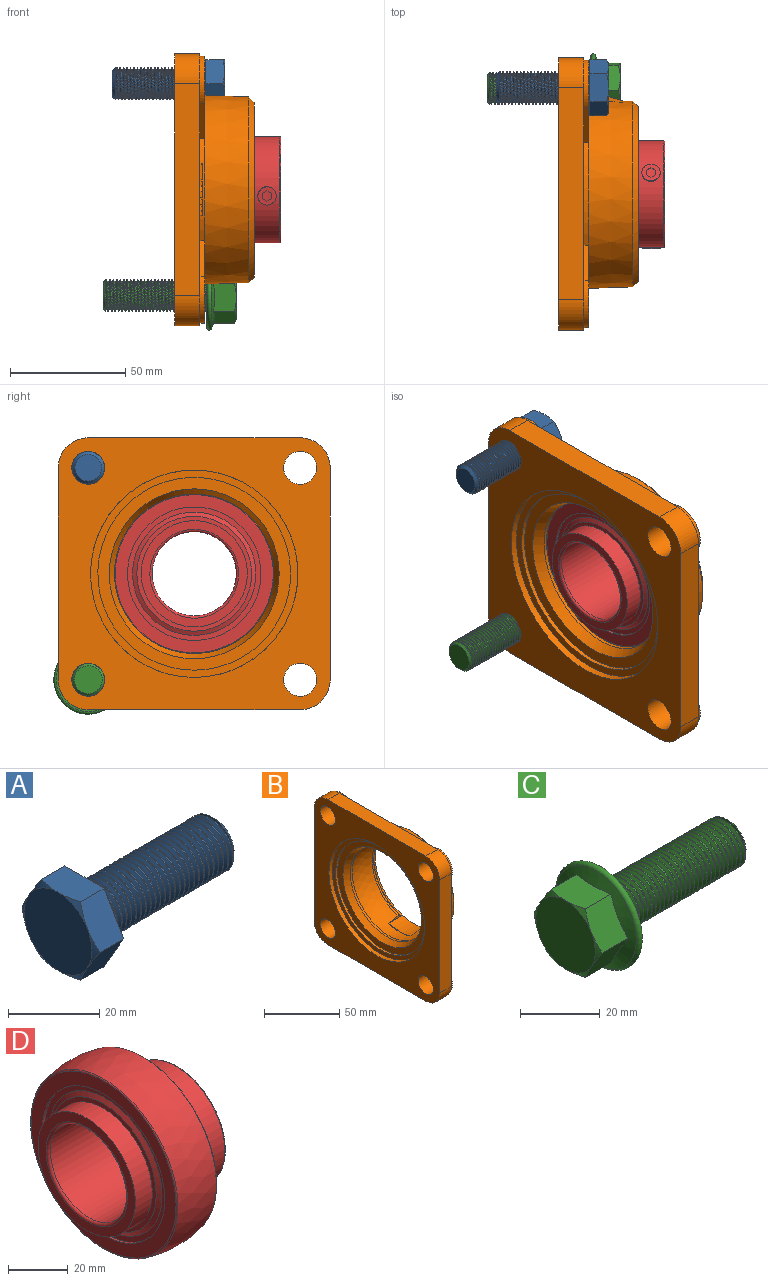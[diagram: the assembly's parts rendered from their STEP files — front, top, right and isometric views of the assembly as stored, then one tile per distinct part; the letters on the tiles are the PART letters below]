
ASSEMBLY  parts=4 mates=3
PART A: 25 faces, bbox 49.8x25.2x25.2 mm
  f0: plane 24.25x21mm, normal (1,0,0), area 87.2mm2, adj f1,f7,f8,f9,f10,f11,f12
  f1: cylinder r=9.68mm len=19.37mm, axis (1,0,0), area 36.5mm2, adj f0,f2
  f2: plane 19.37x19.37mm, normal (1,0,0), area 113.2mm2, adj f1,f3
  f3: torus R=7.6mm, axis (1,0,0), area 42.7mm2, adj f2,f4,f23
  f4: cylinder r=7mm len=38.17mm, axis (1,0,0), area 714.9mm2, adj f3,f5,f21,f22
  f5: cone r=7mm half-angle=45deg, axis (-1,0,0), area 69.6mm2, adj f4,f6,f24
  f6: plane 11.55x11.55mm, normal (1,0,0), area 104.7mm2, adj f5
  f7: plane 13.13x9.2mm, normal (0,0,1), area 95.5mm2, adj f0,f8,f12,f13,f14
  f8: plane 11.5x9.2mm, normal (0,0.87,0.5), area 95.5mm2, adj f0,f7,f9,f13,f17
  f9: plane 11.5x9.2mm, normal (0,0.87,-0.5), area 95.5mm2, adj f0,f8,f10,f16,f17
  f10: plane 13.13x9.2mm, normal (0,0,-1), area 95.5mm2, adj f0,f9,f11,f15,f16
  f11: plane 11.5x9.2mm, normal (0,-0.87,-0.5), area 95.5mm2, adj f0,f10,f12,f15,f19
  f12: plane 11.5x9.2mm, normal (0,-0.87,0.5), area 95.5mm2, adj f0,f7,f11,f14,f19
  f13: cone r=10.5mm half-angle=60deg, axis (1,0,0), area 10.8mm2, adj f7,f8,f18
  f14: cone r=10.5mm half-angle=60deg, axis (1,0,0), area 10.8mm2, adj f7,f12,f18
  f15: cone r=10.5mm half-angle=60deg, axis (1,0,0), area 10.8mm2, adj f10,f11,f18
  f16: cone r=10.5mm half-angle=60deg, axis (1,0,0), area 10.8mm2, adj f9,f10,f18
  f17: cone r=10.5mm half-angle=60deg, axis (1,0,0), area 10.8mm2, adj f8,f9,f18
  f18: plane 21x21mm, normal (-1,0,0), area 346.4mm2, adj f13,f14,f15,f16,f17,f19
  f19: cone r=10.5mm half-angle=60deg, axis (1,0,0), area 10.8mm2, adj f11,f12,f18
  f20: bspline ~39.13x14.29mm, area 409.6mm2, adj f21,f22,f23,f24
  f21: bspline ~39.47x16.17mm, area 983.8mm2, adj f4,f20,f23,f24
  f22: bspline ~39.22x16.17mm, area 995.1mm2, adj f4,f20,f23,f24
  f23: plane 14.46x14.08mm, normal (1,0,0), area 19.7mm2, adj f3,f20,f21,f22
  f24: plane 14.43x14.43mm, normal (-1,0,0), area 19.7mm2, adj f5,f20,f21,f22
PART B: 189 faces, bbox 34.7x118.2x118.2 mm
  f0: cone r=34.38mm half-angle=45deg, axis (1,0,0), area 159.3mm2, adj f2,f4,f183,f185
  f1: cone r=34.38mm half-angle=45deg, axis (1,0,0), area 159.3mm2, adj f3,f5,f182,f188
  f2: cylinder r=35.95mm len=68.8mm, axis (1,0,0), area 131.4mm2, adj f0,f178,f183,f185
  f3: cylinder r=35.95mm len=68.8mm, axis (1,0,0), area 131.4mm2, adj f1,f178,f182,f188
  f4: cylinder r=34.69mm len=66.17mm, axis (-1,0,0), area 122.5mm2, adj f0,f6,f183,f185
  f5: cylinder r=34.69mm len=66.17mm, axis (-1,0,0), area 122.5mm2, adj f1,f6,f182,f188
  f6: sphere r=35.95mm, area 3847.3mm2, adj f4,f5,f180,f181,f182,f183,f185,f186
  f7: cone r=36.85mm half-angle=24.3deg, axis (-1,0,0), area 1179.7mm2, adj f177,f180
  f8: plane 118x118mm, normal (1,0,0), area 4439.2mm2, adj f9,f11,f12,f13,f14,f15,f16,f17
  f9: cylinder r=45.07mm len=15.09mm, axis (1,0,0), area 32.1mm2, adj f8,f34,f36,f41
  f10: cylinder r=45mm len=90mm, axis (-1,0,0), area 904.8mm2, adj f19,f173
  f11: cylinder r=13mm len=13mm, axis (-1,0,0), area 224.7mm2, adj f8,f12,f18,f19
  f12: plane 92x11.01mm, normal (0,0,1), area 1012.5mm2, adj f8,f11,f13,f19
  f13: cylinder r=13mm len=13mm, axis (-1,0,0), area 224.7mm2, adj f8,f12,f14,f19
  f14: plane 92x11.01mm, normal (0,-1,0), area 1012.5mm2, adj f8,f13,f15,f19
  f15: cylinder r=13mm len=13mm, axis (-1,0,0), area 224.7mm2, adj f8,f14,f16,f19
  f16: plane 92x11.01mm, normal (0,0,-1), area 1012.5mm2, adj f8,f15,f17,f19
  f17: cylinder r=13mm len=13mm, axis (-1,0,0), area 224.7mm2, adj f8,f16,f18,f19
  f18: plane 92x11.01mm, normal (0,1,0), area 1012.5mm2, adj f8,f11,f17,f19
  f19: plane 118x118mm, normal (-1,0,0), area 6774.8mm2, adj f10,f11,f12,f13,f14,f15,f16,f17
  f20: plane 15.28x15.28mm, normal (0,0.71,-0.71), area 43.1mm2, adj f8,f21,f35,f36
  f21: cylinder r=12mm len=20.49mm, axis (1,0,0), area 75.2mm2, adj f8,f20,f22,f36
  f22: plane 15.28x15.28mm, normal (0,-0.71,0.71), area 43.1mm2, adj f8,f21,f23,f36
  f23: cylinder r=45.07mm len=44.47mm, axis (1,0,0), area 92.8mm2, adj f8,f22,f24,f36
  f24: plane 15.28x15.28mm, normal (0,0.71,0.71), area 43.1mm2, adj f8,f23,f25,f36
  f25: cylinder r=12mm len=20.49mm, axis (1,0,0), area 75.2mm2, adj f8,f24,f26,f36
  f26: plane 15.28x15.28mm, normal (0,-0.71,-0.71), area 43.1mm2, adj f8,f25,f27,f36
  f27: cylinder r=45.07mm len=44.47mm, axis (1,0,0), area 92.8mm2, adj f8,f26,f28,f36
  f28: plane 15.28x15.28mm, normal (0,-0.71,0.71), area 43.1mm2, adj f8,f27,f29,f36
  f29: cylinder r=12mm len=20.49mm, axis (1,0,0), area 75.2mm2, adj f8,f28,f30,f36
  f30: plane 15.28x15.28mm, normal (0,0.71,-0.71), area 43.1mm2, adj f8,f29,f31,f36
  f31: cylinder r=45.07mm len=44.47mm, axis (1,0,0), area 92.8mm2, adj f8,f30,f32,f36
  f32: plane 15.28x15.28mm, normal (0,-0.71,-0.71), area 43.1mm2, adj f8,f31,f33,f36
  f33: cylinder r=12mm len=20.49mm, axis (1,0,0), area 75.2mm2, adj f8,f32,f34,f36
  f34: plane 15.28x15.28mm, normal (0,0.71,0.71), area 43.1mm2, adj f8,f9,f33,f36
  f35: cylinder r=45.07mm len=15.09mm, axis (1,0,0), area 32.1mm2, adj f8,f20,f36,f40
  f36: plane 116x116mm, normal (1,0,0), area 3281mm2, adj f9,f20,f21,f22,f23,f24,f25,f26
  f37: cylinder r=7.15mm len=14.3mm, axis (-1,0,0), area 584mm2, adj f19,f36
  f38: cylinder r=7.15mm len=14.3mm, axis (-1,0,0), area 584mm2, adj f19,f36
  f39: cylinder r=7.15mm len=14.3mm, axis (-1,0,0), area 584mm2, adj f19,f36
  f40: plane 16.6x5.72mm, normal (0,0,1), area 39.7mm2, adj f8,f35,f36,f42,f43,f175
  f41: plane 16.6x5.72mm, normal (0,0,-1), area 39.7mm2, adj f8,f9,f36,f42,f43,f174
  f42: plane 14.3x0.65mm, normal (1,0,0), area 3.1mm2, adj f40,f41,f43,f174
  f43: plane 16.6x14.3mm, normal (0.29,0.96,0), area 221.4mm2, adj f8,f40,f41,f42,f44,f45,f46
  f44: plane 6.97x0.14mm, normal (1,0,0), area 0.6mm2, adj f43,f45
  f45: cylinder r=45.07mm len=6.97mm, axis (1,0,0), area 2.1mm2, adj f43,f44
  f46: cylinder r=2.8mm len=5.79mm, axis (0.29,0.96,0), area 26.4mm2, adj f43,f47
  f47: plane 5.6x5.36mm, normal (0.29,0.96,0), area 6.3mm2, adj f46,f48
  f48: torus R=2.42mm, axis (0.29,0.96,0), area 9.9mm2, adj f47,f49
  f49: cone r=1.78mm half-angle=32deg, axis (-0.29,-0.96,0), area 12.8mm2, adj f48,f50
  f50: cone r=1mm half-angle=32deg, axis (0.29,0.96,0), area 7.9mm2, adj f49,f51
  f51: torus R=0.68mm, axis (0.29,0.96,0), area 14.5mm2, adj f50,f52
  f52: cone r=1.3mm half-angle=51.3deg, axis (-0.29,-0.96,0), area 0.3mm2, adj f51,f53
  f53: torus R=0.65mm, axis (0.29,0.96,0), area 4.1mm2, adj f52,f54
  f54: plane 1.3x1.24mm, normal (0.29,0.96,0), area 0.5mm2, adj f53,f55
  f55: cylinder r=0.5mm len=1.1mm, axis (0.29,0.96,0), area 1.6mm2, adj f54,f56
  f56: sphere r=0.5mm, area 1.6mm2, adj f55
  f57: cylinder r=0.23mm len=1mm, axis (-1,0,0), area 0.4mm2, adj f8,f58,f170,f171
  f58: plane 1.63x1mm, normal (0,0,1), area 1.6mm2, adj f8,f57,f59,f171
  f59: cylinder r=0.23mm len=1mm, axis (-1,0,0), area 0.4mm2, adj f8,f58,f60,f171
  f60: plane 6.5x1mm, normal (0,-1,0), area 6.5mm2, adj f8,f59,f61,f171
  f61: cylinder r=0.23mm len=1mm, axis (-1,0,0), area 0.4mm2, adj f8,f60,f62,f171
  f62: plane 1x0.46mm, normal (0,-1,0), area 0.5mm2, adj f8,f61,f63,f171
  f63: cylinder r=0.23mm len=1mm, axis (-1,0,0), area 0.4mm2, adj f8,f62,f64,f171
  f64: plane 1.86x1mm, normal (0,-1,0), area 1.8mm2, adj f8,f63,f65,f171
  f65: cylinder r=0.23mm len=1mm, axis (-1,0,0), area 0.4mm2, adj f8,f64,f66,f171
  f66: plane 1.86x1mm, normal (0,0,-1), area 1.8mm2, adj f8,f65,f67,f171
  f67: plane 2.02x2.02mm, normal (0,-0.71,0.71), area 2.8mm2, adj f8,f66,f68,f171
  f68: cylinder r=0.23mm len=1mm, axis (-1,0,0), area 0.2mm2, adj f8,f67,f69,f171
  f69: plane 2.46x1mm, normal (0,-1,0), area 2.4mm2, adj f8,f68,f70,f171
  f70: cylinder r=0.23mm len=1mm, axis (-1,0,0), area 0.4mm2, adj f8,f69,f71,f171
  f71: plane 1x0.72mm, normal (0,-1,0), area 0.7mm2, adj f8,f70,f72,f171
  f72: cylinder r=0.23mm len=1mm, axis (-1,0,0), area 0.4mm2, adj f8,f71,f73,f171
  f73: plane 1.86x1mm, normal (0,-1,0), area 1.8mm2, adj f8,f72,f74,f171
  f74: cylinder r=0.23mm len=1mm, axis (-1,0,0), area 0.4mm2, adj f8,f73,f75,f171
  f75: plane 1.63x1mm, normal (0,0,-1), area 1.6mm2, adj f8,f74,f76,f171
  f76: cylinder r=0.23mm len=1mm, axis (-1,0,0), area 0.4mm2, adj f8,f75,f77,f171
  f77: cylinder r=0.23mm len=1mm, axis (-1,0,0), area 0.4mm2, adj f8,f76,f78,f171
  f78: plane 1x0.23mm, normal (0,0,-1), area 0.2mm2, adj f8,f77,f79,f171
  f79: cylinder r=0.23mm len=1mm, axis (-1,0,0), area 0.4mm2, adj f8,f78,f80,f171
  f80: plane 1x0.83mm, normal (0,-1,0), area 0.8mm2, adj f8,f79,f81,f171
  f81: cylinder r=0.23mm len=1mm, axis (-1,0,0), area 0.2mm2, adj f8,f80,f82,f171
  f82: plane 1x0.1mm, normal (0,-0.71,0.71), area 0.1mm2, adj f8,f81,f83,f171
  f83: cylinder r=0.23mm len=1mm, axis (-1,0,0), area 0.2mm2, adj f8,f82,f84,f171
  f84: plane 1.53x1mm, normal (0,-1,0), area 1.5mm2, adj f8,f83,f85,f171
  f85: cylinder r=0.23mm len=1mm, axis (-1,0,0), area 0.4mm2, adj f8,f84,f86,f171
  f86: plane 1x0.7mm, normal (0,0,-1), area 0.7mm2, adj f8,f85,f87,f171
  f87: cylinder r=0.23mm len=1mm, axis (-1,0,0), area 0.4mm2, adj f8,f86,f88,f171
  f88: plane 1.53x1mm, normal (0,1,0), area 1.5mm2, adj f8,f87,f89,f171
  f89: cylinder r=0.23mm len=1mm, axis (-1,0,0), area 0.2mm2, adj f8,f88,f90,f171
  f90: plane 1x0.1mm, normal (0,0.71,0.71), area 0.1mm2, adj f8,f89,f91,f171
  f91: cylinder r=0.23mm len=1mm, axis (-1,0,0), area 0.2mm2, adj f8,f90,f92,f171
  f92: plane 1x0.83mm, normal (0,1,0), area 0.8mm2, adj f8,f91,f93,f171
  f93: cylinder r=0.23mm len=1mm, axis (-1,0,0), area 0.4mm2, adj f8,f92,f94,f171
  f94: plane 1x0.83mm, normal (0,0,-1), area 0.8mm2, adj f8,f93,f95,f171
  f95: cylinder r=0.33mm len=1mm, axis (-1,0,0), area 0.5mm2, adj f8,f94,f96,f171
  f96: plane 1.99x1mm, normal (0,-1,0), area 2mm2, adj f8,f95,f97,f171
  f97: cylinder r=0.23mm len=1mm, axis (-1,0,0), area 0.4mm2, adj f8,f96,f98,f171
  f98: plane 1x0.23mm, normal (0,0,1), area 0.2mm2, adj f8,f97,f99,f171
  f99: cylinder r=0.23mm len=1mm, axis (-1,0,0), area 0.4mm2, adj f8,f98,f100,f171
  f100: plane 2.32x1mm, normal (0,-1,0), area 2.3mm2, adj f8,f99,f101,f171
  f101: cylinder r=0.23mm len=1mm, axis (-1,0,0), area 0.4mm2, adj f8,f100,f102,f171
  f102: plane 1x0.93mm, normal (0,0,-1), area 0.9mm2, adj f8,f101,f103,f171
  f103: cylinder r=0.23mm len=1mm, axis (-1,0,0), area 0.4mm2, adj f8,f102,f104,f171
  f104: plane 6.73x1mm, normal (0,1,0), area 6.7mm2, adj f8,f103,f105,f171
  f105: cylinder r=0.23mm len=1mm, axis (-1,0,0), area 0.4mm2, adj f8,f104,f106,f171
  f106: plane 1.53x1mm, normal (0,0,1), area 1.5mm2, adj f8,f105,f107,f171
  f107: cylinder r=0.23mm len=1mm, axis (-1,0,0), area 0.2mm2, adj f8,f106,f108,f171
  f108: plane 1x0.07mm, normal (0,-0.71,0.71), area 0.1mm2, adj f8,f107,f109,f171
  f109: cylinder r=0.33mm len=1mm, axis (-1,0,0), area 0.3mm2, adj f8,f108,f110,f171
  f110: plane 1.16x1mm, normal (0,0,1), area 1.2mm2, adj f8,f109,f111,f171
  f111: cylinder r=0.23mm len=1mm, axis (-1,0,0), area 0.2mm2, adj f8,f110,f112,f171
  f112: plane 1x0.1mm, normal (0,0.71,0.71), area 0.1mm2, adj f8,f111,f113,f171
  f113: cylinder r=0.23mm len=1mm, axis (-1,0,0), area 0.2mm2, adj f8,f112,f114,f171
  f114: plane 1.3x1mm, normal (0,0,1), area 1.3mm2, adj f8,f113,f115,f171
  f115: plane 1x0.72mm, normal (0,1,0), area 0.7mm2, adj f8,f114,f116,f171
  f116: plane 1.39x1mm, normal (0,0,-1), area 1.4mm2, adj f8,f115,f117,f171
  f117: cylinder r=0.23mm len=1mm, axis (-1,0,0), area 0.4mm2, adj f8,f116,f118,f171
  f118: plane 1.54x1mm, normal (0,1,0), area 1.5mm2, adj f8,f117,f119,f171
  f119: cylinder r=0.23mm len=1mm, axis (-1,0,0), area 0.2mm2, adj f8,f118,f120,f171
  f120: plane 1.56x1.34mm, normal (0,0.76,-0.65), area 2mm2, adj f8,f119,f121,f171
  f121: plane 1x0.63mm, normal (0,-0.71,-0.71), area 0.9mm2, adj f8,f120,f122,f171
  f122: cylinder r=0.23mm len=1mm, axis (-1,0,0), area 0.2mm2, adj f8,f121,f123,f171
  f123: plane 1.76x1mm, normal (0,-1,0), area 1.8mm2, adj f8,f122,f124,f171
  f124: cylinder r=0.23mm len=1mm, axis (-1,0,0), area 0.4mm2, adj f8,f123,f125,f171
  f125: plane 1x0.93mm, normal (0,0,-1), area 0.9mm2, adj f8,f124,f126,f171
  f126: cylinder r=0.23mm len=1mm, axis (-1,0,0), area 0.4mm2, adj f8,f125,f127,f171
  f127: plane 1.99x1mm, normal (0,1,0), area 2mm2, adj f8,f126,f128,f171
  f128: cylinder r=0.23mm len=1mm, axis (-1,0,0), area 0.2mm2, adj f8,f127,f129,f171
  f129: plane 2.01x1.79mm, normal (0,0.66,0.75), area 2.7mm2, adj f8,f128,f130,f171
  f130: plane 1.86x1mm, normal (0,0,-1), area 1.8mm2, adj f8,f129,f131,f171
  f131: cylinder r=0.23mm len=1mm, axis (-1,0,0), area 0.4mm2, adj f8,f130,f132,f171
  f132: plane 1.86x1mm, normal (0,1,0), area 1.8mm2, adj f8,f131,f133,f171
  f133: cylinder r=0.23mm len=1mm, axis (-1,0,0), area 0.4mm2, adj f8,f132,f134,f171
  f134: plane 1.53x1mm, normal (0,0,1), area 1.5mm2, adj f8,f133,f135,f171
  f135: cylinder r=0.23mm len=1mm, axis (-1,0,0), area 0.2mm2, adj f8,f134,f136,f171
  f136: plane 1x0.1mm, normal (0,-0.71,0.71), area 0.1mm2, adj f8,f135,f137,f171
  f137: cylinder r=0.23mm len=1mm, axis (-1,0,0), area 0.2mm2, adj f8,f136,f138,f171
  f138: plane 1x0.97mm, normal (0,0,1), area 1mm2, adj f8,f137,f139,f171
  f139: cylinder r=0.23mm len=1mm, axis (-1,0,0), area 0.2mm2, adj f8,f138,f140,f171
  f140: plane 1x0.1mm, normal (0,0.71,0.71), area 0.1mm2, adj f8,f139,f141,f171
  f141: cylinder r=0.23mm len=1mm, axis (-1,0,0), area 0.2mm2, adj f8,f140,f142,f171
  f142: plane 1.53x1mm, normal (0,0,1), area 1.5mm2, adj f8,f141,f143,f171
  f143: plane 1x0.46mm, normal (0,1,0), area 0.5mm2, adj f8,f142,f144,f171
  f144: plane 2.79x1mm, normal (0,0,-1), area 2.8mm2, adj f8,f143,f145,f171
  f145: cylinder r=0.23mm len=1mm, axis (-1,0,0), area 0.4mm2, adj f8,f144,f146,f171
  f146: plane 3.71x1mm, normal (0,1,0), area 3.7mm2, adj f8,f145,f147,f171
  f147: cylinder r=0.23mm len=1mm, axis (-1,0,0), area 0.4mm2, adj f8,f146,f148,f171
  f148: plane 1x0.93mm, normal (0,0,-1), area 0.9mm2, adj f8,f147,f149,f171
  f149: cylinder r=0.23mm len=1mm, axis (-1,0,0), area 0.4mm2, adj f8,f148,f150,f171
  f150: plane 1x0.93mm, normal (0,-1,0), area 0.9mm2, adj f8,f149,f151,f171
  f151: cylinder r=0.23mm len=1mm, axis (-1,0,0), area 0.4mm2, adj f8,f150,f152,f171
  f152: plane 1x0.23mm, normal (0,0,1), area 0.2mm2, adj f8,f151,f153,f171
  f153: cylinder r=0.23mm len=1mm, axis (-1,0,0), area 0.4mm2, adj f8,f152,f154,f171
  f154: plane 1.63x1mm, normal (0,-1,0), area 1.6mm2, adj f8,f153,f155,f171
  f155: cylinder r=0.23mm len=1mm, axis (-1,0,0), area 0.4mm2, adj f8,f154,f156,f171
  f156: plane 1x0.86mm, normal (0,0,-1), area 0.9mm2, adj f8,f155,f157,f171
  f157: cylinder r=0.3mm len=1mm, axis (-1,0,0), area 0.5mm2, adj f8,f156,f158,f171
  f158: plane 4.99x1mm, normal (0,1,0), area 5mm2, adj f8,f157,f159,f171
  f159: cylinder r=0.28mm len=1mm, axis (-1,0,0), area 0.4mm2, adj f8,f158,f160,f171
  f160: plane 2.27x1mm, normal (0,0,1), area 2.3mm2, adj f8,f159,f161,f171
  f161: cylinder r=0.23mm len=1mm, axis (-1,0,0), area 0.4mm2, adj f8,f160,f162,f171
  f162: plane 3.71x1mm, normal (0,-1,0), area 3.7mm2, adj f8,f161,f163,f171
  f163: cylinder r=0.23mm len=1mm, axis (-1,0,0), area 0.4mm2, adj f8,f162,f164,f171
  f164: plane 1.63x1mm, normal (0,0,1), area 1.6mm2, adj f8,f163,f165,f171
  f165: cylinder r=0.23mm len=1mm, axis (-1,0,0), area 0.4mm2, adj f8,f164,f166,f171
  f166: plane 2.32x1mm, normal (0,1,0), area 2.3mm2, adj f8,f165,f167,f171
  f167: cylinder r=0.23mm len=1mm, axis (-1,0,0), area 0.4mm2, adj f8,f166,f168,f171
  f168: plane 1x0.93mm, normal (0,0,-1), area 0.9mm2, adj f8,f167,f169,f171
  f169: cylinder r=0.23mm len=1mm, axis (-1,0,0), area 0.4mm2, adj f8,f168,f170,f171
  f170: plane 1.63x1mm, normal (0,1,0), area 1.6mm2, adj f8,f57,f169,f171
  f171: plane 22.54x5.57mm, normal (1,0,0), area 73.4mm2, adj f57,f58,f59,f60,f61,f62,f63,f64
  f172: cylinder r=7.15mm len=14.3mm, axis (-1,0,0), area 584mm2, adj f19,f36
  f173: plane 90x90mm, normal (-1,0,0), area 862.3mm2, adj f10,f176
  f174: cone r=40.3mm half-angle=2deg, axis (-1,0,0), area 4716.6mm2, adj f36,f41,f42,f175,f179
  f175: cone r=40.3mm half-angle=2deg, axis (-1,0,0), area 0.7mm2, adj f36,f40,f174
  f176: cylinder r=41.84mm len=83.68mm, axis (1,0,0), area 479.8mm2, adj f173,f177
  f177: plane 83.68x83.68mm, normal (-1,0,0), area 1232.3mm2, adj f7,f176
  f178: plane 76.18x76.18mm, normal (1,0,0), area 495.2mm2, adj f2,f3,f179,f182,f183,f184,f185,f187
  f179: cone r=38.09mm half-angle=45deg, axis (-1,0,0), area 771.5mm2, adj f174,f178
  f180: cylinder r=34.69mm len=69.39mm, axis (-1,0,0), area 386.9mm2, adj f6,f7
  f181: plane 20.9x1.6mm, normal (1,0,0), area 1.1mm2, adj f6,f182,f183,f184
  f182: plane 13.7x1.57mm, normal (0,1,0), area 7.5mm2, adj f1,f3,f5,f6,f178,f181,f184
  f183: plane 13.7x1.57mm, normal (0,-1,0), area 7.5mm2, adj f0,f2,f4,f6,f178,f181,f184
  f184: cylinder r=36mm len=20.9mm, axis (-1,0,0), area 286.3mm2, adj f178,f181,f182,f183
  f185: plane 13.7x1.57mm, normal (0,-1,0), area 7.5mm2, adj f0,f2,f4,f6,f178,f186,f187
  f186: plane 20.9x1.6mm, normal (1,0,0), area 1.1mm2, adj f6,f185,f187,f188
  f187: cylinder r=36mm len=20.9mm, axis (-1,0,0), area 286.3mm2, adj f178,f185,f186,f188
  f188: plane 13.7x1.57mm, normal (0,1,0), area 7.5mm2, adj f1,f3,f5,f6,f178,f186,f187
PART C: 25 faces, bbox 58.8x33.4x33.4 mm
  f0: plane 27.8x27.8mm, normal (1,0,0), area 425.5mm2, adj f1,f6
  f1: torus R=7.6mm, axis (1,0,0), area 42.7mm2, adj f0,f2,f23
  f2: cylinder r=7mm len=43.48mm, axis (1,0,0), area 664.9mm2, adj f1,f3,f21,f22
  f3: cone r=7mm half-angle=45deg, axis (-1,0,0), area 53.5mm2, adj f2,f4,f24
  f4: plane 12.16x12.16mm, normal (1,0,0), area 116.1mm2, adj f3
  f5: cone r=0mm half-angle=70deg, axis (1,0,0), area 273.3mm2, adj f6,f7,f8,f9,f10,f11,f12
  f6: torus R=13.9mm, axis (1,0,0), area 269.5mm2, adj f0,f5
  f7: plane 11.5x10.98mm, normal (0,-0.87,0.5), area 112.5mm2, adj f5,f8,f12,f13,f18
  f8: plane 11.5x10.98mm, normal (0,-0.87,-0.5), area 112.5mm2, adj f5,f7,f9,f17,f18
  f9: plane 13.13x10.99mm, normal (0,0,-1), area 112.5mm2, adj f5,f8,f10,f16,f17
  f10: plane 11.5x10.98mm, normal (0,0.87,-0.5), area 112.5mm2, adj f5,f9,f11,f15,f16
  f11: plane 11.5x10.98mm, normal (0,0.87,0.5), area 112.5mm2, adj f5,f10,f12,f14,f15
  f12: plane 13.13x10.99mm, normal (0,0,1), area 112.5mm2, adj f5,f7,f11,f13,f14
  f13: cone r=10.5mm half-angle=60deg, axis (1,0,0), area 10.8mm2, adj f7,f12,f19
  f14: cone r=10.5mm half-angle=60deg, axis (1,0,0), area 10.8mm2, adj f11,f12,f19
  f15: cone r=10.5mm half-angle=60deg, axis (1,0,0), area 10.8mm2, adj f10,f11,f19
  f16: cone r=10.5mm half-angle=60deg, axis (1,0,0), area 10.8mm2, adj f9,f10,f19
  f17: cone r=10.5mm half-angle=60deg, axis (1,0,0), area 10.8mm2, adj f8,f9,f19
  f18: cone r=10.5mm half-angle=60deg, axis (1,0,0), area 10.8mm2, adj f7,f8,f19
  f19: plane 21x21mm, normal (-1,0,0), area 346.4mm2, adj f13,f14,f15,f16,f17,f18
  f20: bspline ~44.63x14.29mm, area 466.9mm2, adj f21,f22,f23,f24
  f21: bspline ~44.72x16.17mm, area 1125.2mm2, adj f2,f20,f23,f24
  f22: bspline ~44.47x16.17mm, area 1131.5mm2, adj f2,f20,f23,f24
  f23: plane 14.45x14.42mm, normal (1,0,0), area 19.7mm2, adj f1,f20,f21,f22
  f24: plane 14.43x14.43mm, normal (-1,0,0), area 19.7mm2, adj f3,f20,f21,f22
PART D: 39 faces, bbox 42.9x75.4x75.4 mm
  f0: cylinder r=23.05mm len=46.1mm, axis (1,0,0), area 2130.8mm2, adj f6,f7,f27,f36
  f1: plane 46.1x46.1mm, normal (-1,0,0), area 504.2mm2, adj f2,f20
  f2: torus R=19.26mm, axis (1,0,0), area 183.8mm2, adj f1,f3
  f3: cylinder r=18.26mm len=40.9mm, axis (1,0,0), area 4691.5mm2, adj f2,f4
  f4: torus R=19.26mm, axis (1,0,0), area 183.8mm2, adj f3,f5
  f5: plane 45.1x45.1mm, normal (1,0,0), area 432.6mm2, adj f4,f6
  f6: torus R=22.55mm, axis (1,0,0), area 112.9mm2, adj f0,f5
  f7: plane 49.8x49.8mm, normal (1,0,0), area 278.7mm2, adj f0,f8
  f8: cone r=24.9mm half-angle=62.8deg, axis (-1,0,0), area 337.5mm2, adj f7,f9
  f9: plane 57.94x57.94mm, normal (1,0,0), area 389mm2, adj f8,f10
  f10: cylinder r=28.97mm len=57.94mm, axis (1,0,0), area 172.9mm2, adj f9,f11
  f11: plane 68.68x68.68mm, normal (1,0,0), area 1067.7mm2, adj f10,f12
  f12: torus R=34.34mm, axis (1,0,0), area 143mm2, adj f11,f13
  f13: sphere r=36mm, area 4128.8mm2, adj f12,f14
  f14: torus R=34.34mm, axis (1,0,0), area 143mm2, adj f13,f15
  f15: plane 68.68x68.68mm, normal (-1,0,0), area 1067.7mm2, adj f14,f16
  f16: cylinder r=28.97mm len=57.94mm, axis (1,0,0), area 172.9mm2, adj f15,f17
  f17: plane 57.94x57.94mm, normal (-1,0,0), area 389mm2, adj f16,f18
  f18: cone r=26.75mm half-angle=62.8deg, axis (1,0,0), area 337.5mm2, adj f17,f19
  f19: plane 49.8x49.8mm, normal (-1,0,0), area 278.7mm2, adj f18,f20
  f20: cylinder r=23.05mm len=46.1mm, axis (1,0,0), area 1158.6mm2, adj f1,f19
  f21: plane 2.29x0.51mm, normal (1,0,0), area 1.1mm2, adj f22,f26,f28,f29
  f22: plane 1.99x1.15mm, normal (0.5,0,0.87), area 1.3mm2, adj f21,f23,f28,f29
  f23: plane 1.99x1.15mm, normal (-0.5,0,0.87), area 1.3mm2, adj f22,f24,f28,f29
  f24: plane 2.29x0.51mm, normal (-1,0,0), area 1.1mm2, adj f23,f25,f28,f29
  f25: plane 1.99x1.15mm, normal (-0.5,0,-0.87), area 1.3mm2, adj f24,f26,f28,f29
  f26: plane 1.99x1.15mm, normal (0.5,0,-0.87), area 1.3mm2, adj f21,f25,f28,f29
  f27: cylinder r=3.97mm len=7.94mm, axis (0,-1,0), area 16.2mm2, adj f0,f28
  f28: plane 7.94x7.94mm, normal (0,1,0), area 35.8mm2, adj f21,f22,f23,f24,f25,f26,f27
  f29: cylinder r=23.05mm len=4.58mm, axis (1,0,0), area 13.7mm2, adj f21,f22,f23,f24,f25,f26
  f30: plane 2.24x1.59mm, normal (1,0,0), area 1.1mm2, adj f32,f35,f37,f38
  f31: plane 2.24x1.59mm, normal (-1,0,0), area 1.1mm2, adj f33,f34,f37,f38
  f32: plane 1.99x1.25mm, normal (0.5,0.75,-0.43), area 1.3mm2, adj f30,f33,f37,f38
  f33: plane 1.99x1.25mm, normal (-0.5,0.75,-0.43), area 1.3mm2, adj f31,f32,f37,f38
  f34: plane 1.99x1.29mm, normal (-0.5,-0.75,0.43), area 1.3mm2, adj f31,f35,f37,f38
  f35: plane 1.99x1.29mm, normal (0.5,-0.75,0.43), area 1.3mm2, adj f30,f34,f37,f38
  f36: cylinder r=3.97mm len=7.94mm, axis (0,0.5,0.87), area 16.2mm2, adj f0,f37
  f37: plane 7.94x6.87mm, normal (0,-0.5,-0.87), area 35.8mm2, adj f30,f31,f32,f33,f34,f35,f36
  f38: cylinder r=23.05mm len=3.97mm, axis (1,0,0), area 13.7mm2, adj f30,f31,f32,f33,f34,f35
PLACE A rot(axis=(0,0,1),180deg) t=(-76.98,12.97,59.44)mm
PLACE B t=(-68.98,-33.03,13.44)mm fixed
PLACE C rot(axis=(0,-0.29,0.96),180deg) t=(-75.96,12.97,-32.56)mm
PLACE D rot(axis=(-1,0,0),173.4deg) t=(-69.27,-33.03,13.44)mm
MATE cylindrical C.f1 <-> B.f17  axis (-1,0,0) through (-75.96,12.97,-32.56)mm
MATE fastened A.f1 <-> B.f11  axis (-1,0,0) through (-76.98,12.97,59.44)mm
MATE revolute D.f0 <-> B.f0  axis (1,0,0) through (-78.4,-33.03,13.44)mm
